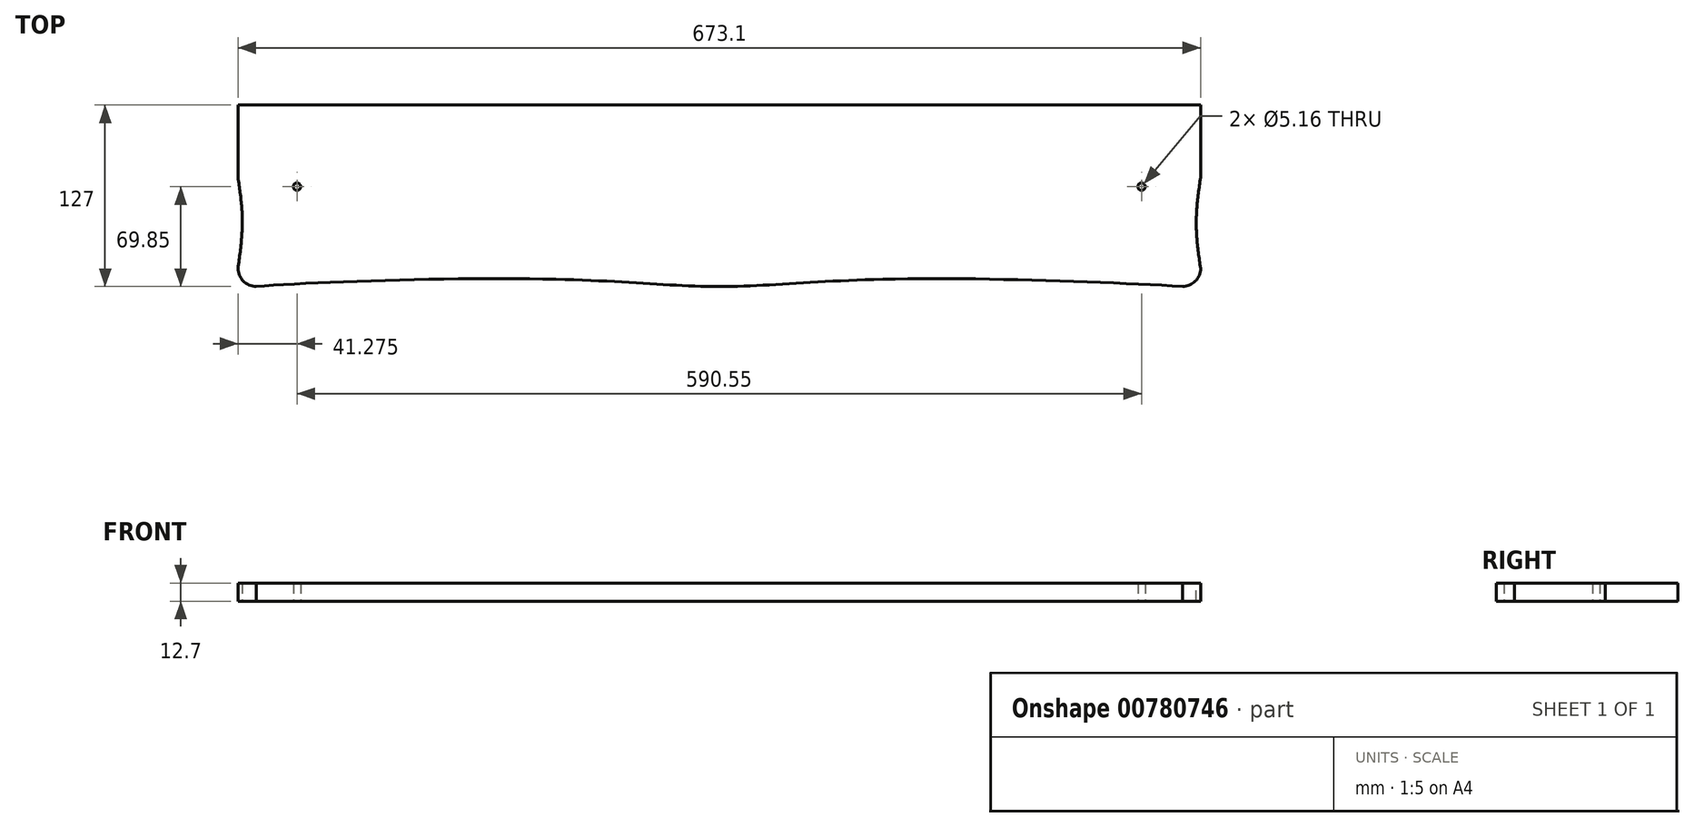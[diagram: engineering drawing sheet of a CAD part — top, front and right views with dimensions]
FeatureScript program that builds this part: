
annotation { "Feature Type Name" : "Feature", "Feature Type Description" : "" }
export const myFeature = defineFeature(function(context is Context, id is Id, definition is map)
    precondition{}
    {
        {
            var Q0;
            Q0=qCreatedBy(makeId("Top.planeOp"),FACE);
            var sketch = newSketch(context, id + "F0", { "sketchPlane" : qUnion([Q0])});
            skLineSegment(sketch, "E0.bottom", {"start": v(-673.1, 127) * mm, "end": v(0, 127) * mm});
            skLineSegment(sketch, "E0.top", {"start": v(-673.1, 0) * mm, "end": v(0, 0) * mm});
            skLineSegment(sketch, "E0.left", {"start": v(-673.1, 127) * mm, "end": v(-673.1, 0) * mm});
            skLineSegment(sketch, "E0.right", {"start": v(0, 127) * mm, "end": v(0, 0) * mm});
            skSolve(sketch);
        }
        {
            var Q0;
            Q0=makeQuery(id+"F0.imprint","IMPRINT",FACE,{"disambiguationData":[TD([[makeQuery(id+"F0.imprint","IMPRINT",EDGE,{"derivedFrom":sQuery(id+"F0.wireOp",EDGE,"E0.bottom")}),-1.0]])]});
            extrude(context, id + "F1", {"entities" : qUnion([Q0]), "depth" : 12.7 * mm});
        }
        {
            var Q0;
            Q0=makeQuery(id+"F1.opExtrude","CAP_FACE",FACE,{"disambiguationData":[OSD([sQuery(id+"F0.wireOp",EDGE,"E0.bottom"),sQuery(id+"F0.wireOp",EDGE,"E0.top"),sQuery(id+"F0.wireOp",EDGE,"E0.left"),sQuery(id+"F0.wireOp",EDGE,"E0.right")])],"isStart":false});
            var sketch = newSketch(context, id + "F2", { "sketchPlane" : qUnion([Q0])});
            skPoint(sketch, "E1", {"position": v(-673.1, 12.7) * mm});
            skPoint(sketch, "E2", {"position": v(-660.4, 0) * mm});
            skPoint(sketch, "E3", {"position": v(0, 12.7) * mm});
            skPoint(sketch, "E4", {"position": v(-12.7, 0) * mm});
            skPoint(sketch, "E5", {"position": v(-336.55, 0) * mm});
            skPoint(sketch, "E6", {"position": v(-450.85, 0) * mm});
            skPoint(sketch, "E7", {"position": v(-222.25, 0) * mm});
            skLineSegment(sketch, "E8", {"start": v(-450.85, 0) * mm, "end": v(-450.85, 5.08) * mm});
            skLineSegment(sketch, "E9", {"start": v(-222.25, 0) * mm, "end": v(-222.25, 5.08) * mm});
            skFitSpline(sketch, "E10", {"points": [v(-660.4, 0) * mm, v(-450.85, 5.08) * mm, v(-336.55, 0) * mm, v(-222.25, 5.08) * mm, v(-12.7, 0) * mm], "startDerivative": vector(437.89, 35.64) * mm, "endDerivative": vector(553.7, -34.24) * mm});
            skPoint(sketch, "E11", {"position": v(-673.1, 45.72) * mm});
            skPoint(sketch, "E12", {"position": v(0, 44.43) * mm});
            skLineSegment(sketch, "E13", {"start": v(-673.1, 45.72) * mm, "end": v(-670.05, 45.72) * mm});
            skLineSegment(sketch, "E14", {"start": v(0, 44.43) * mm, "end": v(-3.05, 44.43) * mm});
            skPoint(sketch, "E15", {"position": v(0, 76.2) * mm});
            skPoint(sketch, "E16", {"position": v(-673.1, 76.2) * mm});
            skFitSpline(sketch, "E17", {"points": [v(-673.1, 76.2) * mm, v(-670.05, 45.72) * mm, v(-673.1, 12.7) * mm], "startDerivative": vector(9.2, -61.56) * mm, "endDerivative": vector(-9.09, -65.4) * mm});
            skFitSpline(sketch, "E18", {"points": [v(0, 76.2) * mm, v(-3.05, 44.43) * mm, v(0, 12.7) * mm], "startDerivative": vector(-9.14, -63.53) * mm, "endDerivative": vector(9.15, -63.47) * mm});
            skPoint(sketch, "E19", {"position": v(-336.55, 127) * mm});
            skSolve(sketch);
        }
        {
            var Q0;
            {var subQ0=sQuery(id+"F2.wireOp",EDGE,"E8");Q0=makeQuery(id+"F2.imprint","IMPRINT",FACE,{"disambiguationData":[TD([[makeQuery(id+"F2.imprint","IMPRINT",EDGE,{"derivedFrom":subQ0}),1.0]])]});}
            var Q1;
            {var subQ0=sQuery(id+"F2.wireOp",EDGE,"E8");Q1=makeQuery(id+"F2.imprint","IMPRINT",FACE,{"disambiguationData":[TD([[makeQuery(id+"F2.imprint","IMPRINT",EDGE,{"derivedFrom":subQ0}),-1.0]])]});}
            var Q2;
            {var subQ0=sQuery(id+"F2.wireOp",EDGE,"E9");Q2=makeQuery(id+"F2.imprint","IMPRINT",FACE,{"disambiguationData":[TD([[makeQuery(id+"F2.imprint","IMPRINT",EDGE,{"derivedFrom":subQ0}),1.0]])]});}
            var Q3;
            {var subQ0=sQuery(id+"F2.wireOp",EDGE,"E9");Q3=makeQuery(id+"F2.imprint","IMPRINT",FACE,{"disambiguationData":[TD([[makeQuery(id+"F2.imprint","IMPRINT",EDGE,{"derivedFrom":subQ0}),-1.0]])]});}
            var Q4;
            {var subQ0=sQuery(id+"F2.wireOp",EDGE,"E14");Q4=makeQuery(id+"F2.imprint","IMPRINT",FACE,{"disambiguationData":[TD([[makeQuery(id+"F2.imprint","IMPRINT",EDGE,{"derivedFrom":subQ0}),-1.0]])]});}
            var Q5;
            {var subQ0=sQuery(id+"F2.wireOp",EDGE,"E14");Q5=makeQuery(id+"F2.imprint","IMPRINT",FACE,{"disambiguationData":[TD([[makeQuery(id+"F2.imprint","IMPRINT",EDGE,{"derivedFrom":subQ0}),1.0]])]});}
            var Q6;
            {var subQ0=sQuery(id+"F2.wireOp",EDGE,"E13");Q6=makeQuery(id+"F2.imprint","IMPRINT",FACE,{"disambiguationData":[TD([[makeQuery(id+"F2.imprint","IMPRINT",EDGE,{"derivedFrom":subQ0}),1.0]])]});}
            var Q7;
            {var subQ0=sQuery(id+"F2.wireOp",EDGE,"E13");Q7=makeQuery(id+"F2.imprint","IMPRINT",FACE,{"disambiguationData":[TD([[makeQuery(id+"F2.imprint","IMPRINT",EDGE,{"derivedFrom":subQ0}),-1.0]])]});}
            extrude(context, id + "F3", {"entities" : qUnion([Q0, Q1, Q2, Q3, Q4, Q5, Q6, Q7]), "operationType" : NewBodyOperationType.REMOVE, "oppositeDirection" : true, "depth" : 12.7 * mm, "offsetDistance" : 25.4 * mm});
        }
        {
            var Q0;
            Q0=makeQuery(id+"F1.opExtrude","SWEPT_EDGE",EDGE,{"disambiguationData":[OSD([sQuery(id+"F0.wireOp",EDGE,"E0.top"),sQuery(id+"F0.wireOp",EDGE,"E0.left")])]});
            var Q1;
            Q1=makeQuery(id+"F1.opExtrude","SWEPT_EDGE",EDGE,{"disambiguationData":[OSD([sQuery(id+"F0.wireOp",EDGE,"E0.top"),sQuery(id+"F0.wireOp",EDGE,"E0.right")])]});
            fillet(context, id + "F4", {"entities" : qUnion([Q0, Q1]), "radius" : 12.7 * mm, "tangentPropagation" : true, "allowEdgeOverflow" : false});
        }
        {
            var Q0;
            Q0=makeQuery(id+"F1.opExtrude","CAP_FACE",FACE,{"disambiguationData":[OSD([sQuery(id+"F0.wireOp",EDGE,"E0.bottom"),sQuery(id+"F0.wireOp",EDGE,"E0.top"),sQuery(id+"F0.wireOp",EDGE,"E0.left"),sQuery(id+"F0.wireOp",EDGE,"E0.right")])],"isStart":true});
            var sketch = newSketch(context, id + "F5", { "sketchPlane" : qUnion([Q0])});
            skPoint(sketch, "E20", {"position": v(-41.28, -127) * mm});
            skPoint(sketch, "E21", {"position": v(-631.83, -127) * mm});
            skPoint(sketch, "E22", {"position": v(-336.55, -127) * mm});
            skLineSegment(sketch, "E23", {"start": v(-631.83, -127) * mm, "end": v(-631.83, -69.85) * mm});
            skLineSegment(sketch, "E24", {"start": v(-41.28, -127) * mm, "end": v(-41.28, -69.85) * mm});
            skCircle(sketch, "E25", {"center": v(-631.83, -69.85) * mm, "radius": 2.58 * mm});
            skCircle(sketch, "E26", {"center": v(-41.28, -69.85) * mm, "radius": 2.58 * mm});
            skSolve(sketch);
        }
        {
            var Q0;
            Q0=makeQuery(id+"F5.imprint","IMPRINT",FACE,{"disambiguationData":[TD([[makeQuery(id+"F5.imprint","IMPRINT",EDGE,{"derivedFrom":sQuery(id+"F5.wireOp",EDGE,"E26")}),1.0]])]});
            var Q1;
            Q1=makeQuery(id+"F5.imprint","IMPRINT",FACE,{"disambiguationData":[TD([[makeQuery(id+"F5.imprint","IMPRINT",EDGE,{"derivedFrom":sQuery(id+"F5.wireOp",EDGE,"E25")}),1.0]])]});
            extrude(context, id + "F6", {"entities" : qUnion([Q0, Q1]), "operationType" : NewBodyOperationType.REMOVE, "oppositeDirection" : true, "depth" : 12.7 * mm, "offsetDistance" : 25.4 * mm});
        }
    });
